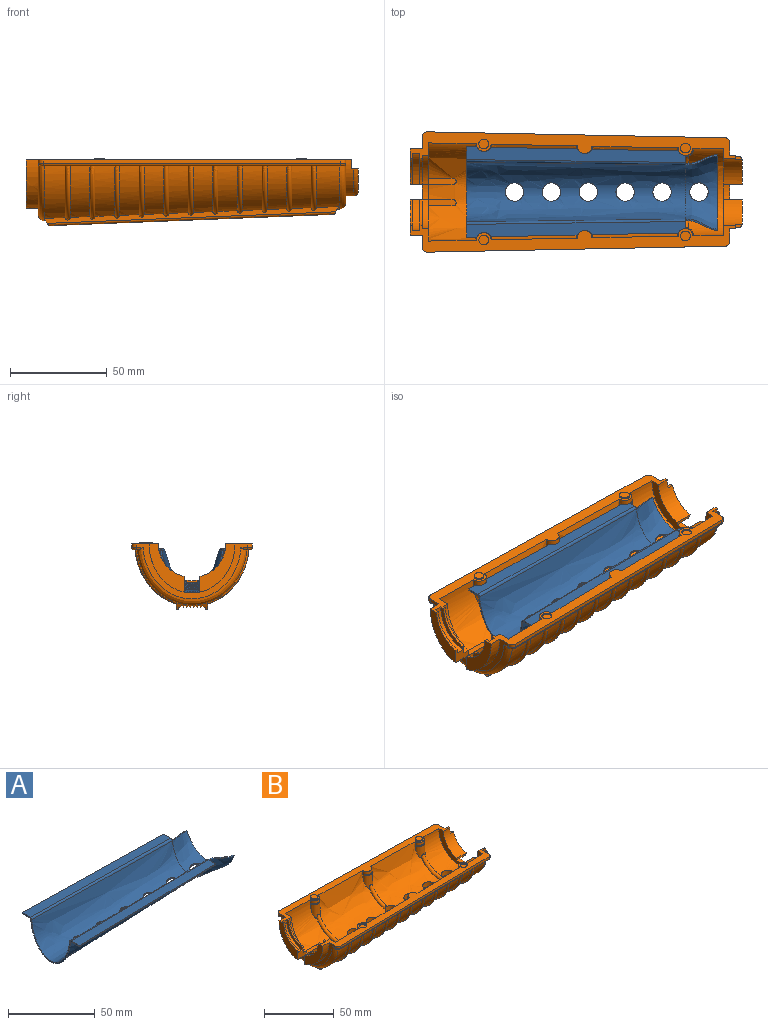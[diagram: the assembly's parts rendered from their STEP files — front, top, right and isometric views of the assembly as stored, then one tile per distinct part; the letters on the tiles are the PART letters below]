
ASSEMBLY  parts=2 mates=1
PART A: 31 faces, bbox 177.5x65.5x54.2 mm
  f0: bspline ~152.4x63.95mm, area 5551mm2, adj f2,f15,f23,f24,f26,f27,f28,f29
  f1: offset ~39.16x18.48mm, area 778.8mm2, adj f7,f8,f9,f25
  f2: bspline ~37.57x16.92mm, area 743.3mm2, adj f0,f7,f8,f9,f25
  f3: plane 6.64x0.79mm, normal (-1,0,0), area 5.3mm2, adj f4,f16,f18,f22
  f4: plane 113.03x2.26mm, normal (0.02,1,0), area 89.7mm2, adj f3,f5,f18,f22
  f5: plane 5.85x0.79mm, normal (1,0,0), area 4.6mm2, adj f4,f6,f18,f22
  f6: bspline ~1.26x1.21mm, area 1mm2, adj f5,f7,f20,f24
  f7: bspline ~16.51x5.3mm, area 14.1mm2, adj f1,f2,f6,f8
  f8: plane 39.09x15.21mm, normal (1,0,0), area 40.2mm2, adj f1,f2,f7,f9
  f9: bspline ~16.51x5.82mm, area 14mm2, adj f1,f2,f8,f10
  f10: bspline ~1.26x1.21mm, area 1mm2, adj f9,f11,f19,f23
  f11: plane 5.84x0.79mm, normal (1,0,0), area 4.6mm2, adj f10,f12,f17,f21
  f12: plane 113.03x2.26mm, normal (0.02,-1,0), area 89.7mm2, adj f11,f13,f17,f21
  f13: plane 6.63x0.79mm, normal (-1,0,0), area 5.3mm2, adj f12,f14,f17,f21
  f14: bspline ~1.26x1.23mm, area 1mm2, adj f13,f15,f19,f23
  f15: bspline ~32.49x21.92mm, area 46.1mm2, adj f0,f14,f16
  f16: bspline ~1.26x1.23mm, area 1mm2, adj f3,f15,f20,f24
  f17: plane 113.03x8.1mm, normal (0,0,-1), area 704.9mm2, adj f11,f12,f13,f19
  f18: plane 113.03x8.11mm, normal (0,0,-1), area 705.5mm2, adj f3,f4,f5,f20
  f19: bspline ~156.83x2.51mm, area 78.8mm2, adj f10,f14,f17
  f20: bspline ~156.83x2.51mm, area 78.7mm2, adj f6,f16,f18
  f21: plane 113.03x8.1mm, normal (0,0,1), area 704.9mm2, adj f11,f12,f13,f23
  f22: plane 113.03x8.11mm, normal (0,0,1), area 705.5mm2, adj f3,f4,f5,f24
  f23: bspline ~156.84x3.3mm, area 210.1mm2, adj f0,f10,f14,f21
  f24: bspline ~156.84x3.3mm, area 209.9mm2, adj f0,f6,f16,f22
  f25: cylinder r=4.76mm len=9.53mm, axis (0,0,1), area 24.6mm2, adj f1,f2
  f26: cylinder r=4.76mm len=9.53mm, axis (0,0,1), area 25.1mm2, adj f0
  f27: cylinder r=4.76mm len=9.53mm, axis (0,0,1), area 25.1mm2, adj f0
  f28: cylinder r=4.76mm len=9.53mm, axis (0,0,1), area 25.1mm2, adj f0
  f29: cylinder r=4.76mm len=9.53mm, axis (0,0,1), area 25.1mm2, adj f0
  f30: cylinder r=4.76mm len=9.53mm, axis (0,0,1), area 25.1mm2, adj f0
PART B: 246 faces, bbox 229.3x149.4x113.7 mm
  f0: cylinder r=17.46mm len=17.01mm, axis (1,0,0), area 29.8mm2, adj f13,f41,f198,f243
  f1: cylinder r=17.46mm len=17.01mm, axis (1,0,0), area 29.8mm2, adj f12,f137,f199,f242
  f2: cone r=3.81mm half-angle=3deg, axis (0,0,-1), area 122.1mm2, adj f13,f15,f40,f204,f237,f238,f239
  f3: cone r=3.81mm half-angle=3deg, axis (0,0,-1), area 132.4mm2, adj f13,f14,f15,f39,f234,f235,f236
  f4: cone r=3.81mm half-angle=3deg, axis (0,0,-1), area 142.5mm2, adj f8,f13,f14,f205,f231,f232,f233
  f5: cone r=3.81mm half-angle=3deg, axis (0,0,-1), area 142.5mm2, adj f8,f12,f14,f205,f228,f229,f230
  f6: cone r=3.81mm half-angle=3deg, axis (0,0,-1), area 132.4mm2, adj f12,f14,f15,f38,f225,f226,f227
  f7: cone r=3.81mm half-angle=3deg, axis (0,0,-1), area 122.1mm2, adj f12,f15,f40,f204,f222,f223,f224
  f8: offset ~81.13x59.72mm, area 2868.9mm2, adj f4,f5,f9,f10,f11,f12,f13,f199
  f9: plane 8.31x3.82mm, normal (1,0,0), area 24.3mm2, adj f8,f197,f199,f217
  f10: plane 28.95x23.02mm, normal (1,0,0), area 200.2mm2, adj f8,f12,f144,f199,f220,f221
  f11: plane 85.09x79.17mm, normal (1,0,0), area 200.2mm2, adj f8,f13,f44,f198,f215,f218
  f12: plane 224.2x69.53mm, normal (0,0,1), area 994.6mm2, adj f1,f5,f6,f7,f8,f10,f14,f15
  f13: plane 226.06x71.39mm, normal (0,0,1), area 994.6mm2, adj f0,f2,f3,f4,f8,f11,f14,f15
  f14: offset ~79.55x57.68mm, area 4950.3mm2, adj f3,f4,f5,f6,f12,f13,f38,f39
  f15: offset ~76.82x55.29mm, area 4608.6mm2, adj f2,f3,f6,f7,f12,f13,f38,f39
  f16: plane 150.68x7.49mm, normal (0.03,-0.71,-0.71), area 182mm2, adj f18,f19,f71,f72,f91,f101,f111,f159
  f17: plane 150.7x7.51mm, normal (0.03,0.71,-0.71), area 181.7mm2, adj f36,f37,f89,f90,f100,f110,f120,f159
  f18: plane 15.79x1.59mm, normal (0.03,0.71,-0.71), area 17.6mm2, adj f16,f21,f173,f206
  f19: plane 15.79x1.59mm, normal (0.03,0.71,-0.71), area 17.6mm2, adj f16,f20,f174,f206
  f20: plane 12.78x1.42mm, normal (0.03,-0.71,-0.71), area 14.9mm2, adj f19,f23,f174,f206
  f21: plane 12.78x1.42mm, normal (0.03,-0.71,-0.71), area 14.9mm2, adj f18,f22,f173,f206
  f22: plane 11.19x1.34mm, normal (0.03,0.71,-0.71), area 13.4mm2, adj f21,f25,f173,f206
  f23: plane 11.19x1.34mm, normal (0.03,0.71,-0.71), area 13.4mm2, adj f20,f24,f174,f206
  f24: plane 10.23x1.3mm, normal (0.03,-0.71,-0.71), area 12.5mm2, adj f23,f27,f174,f206
  f25: plane 10.23x1.3mm, normal (0.03,-0.71,-0.71), area 12.5mm2, adj f22,f26,f173,f206
  f26: plane 9.7x1.28mm, normal (0.03,0.71,-0.71), area 12.1mm2, adj f25,f29,f173,f206
  f27: plane 9.7x1.28mm, normal (0.03,0.71,-0.71), area 12.1mm2, adj f24,f28,f174,f206
  f28: plane 9.7x1.28mm, normal (0.03,-0.71,-0.71), area 12mm2, adj f27,f31,f174,f206
  f29: plane 9.7x1.28mm, normal (0.03,-0.71,-0.71), area 12mm2, adj f26,f30,f173,f206
  f30: plane 10.22x1.3mm, normal (0.03,0.71,-0.71), area 12.5mm2, adj f29,f33,f173,f206
  f31: plane 10.22x1.3mm, normal (0.03,0.71,-0.71), area 12.5mm2, adj f28,f32,f174,f206
  f32: plane 11.18x1.34mm, normal (0.03,-0.71,-0.71), area 13.4mm2, adj f31,f35,f174,f206
  f33: plane 11.18x1.34mm, normal (0.03,-0.71,-0.71), area 13.4mm2, adj f30,f34,f173,f206
  f34: plane 12.75x1.42mm, normal (0.03,0.71,-0.71), area 14.9mm2, adj f33,f37,f173,f206
  f35: plane 12.75x1.42mm, normal (0.03,0.71,-0.71), area 14.9mm2, adj f32,f36,f174,f206
  f36: plane 15.74x1.59mm, normal (0.03,-0.71,-0.71), area 17.6mm2, adj f17,f35,f174,f206
  f37: plane 15.74x1.59mm, normal (0.03,-0.71,-0.71), area 17.6mm2, adj f17,f34,f173,f206
  f38: bspline ~21.22x16.17mm, area 99.1mm2, adj f6,f14,f15,f206
  f39: bspline ~22.14x18.27mm, area 99.1mm2, adj f3,f14,f15,f206
  f40: offset ~74.08x50.66mm, area 1618.4mm2, adj f2,f7,f12,f13,f145,f171,f204
  f41: plane 25.12x18.33mm, normal (-1,0,0), area 172.2mm2, adj f0,f13,f42,f198
  f42: extruded ~24.99x18.26mm, area 212.3mm2, adj f13,f41,f139,f198
  f43: cylinder r=17.46mm len=17.01mm, axis (1,0,0), area 29.8mm2, adj f13,f45,f198,f244
  f44: extruded ~21.73x15.08mm, area 90.3mm2, adj f11,f13,f45,f198
  f45: plane 21.77x15.1mm, normal (1,0,0), area 73.9mm2, adj f13,f43,f44,f198
  f46: cylinder r=19.05mm len=18.63mm, axis (-1,0,0), area 104.4mm2, adj f12,f48,f140,f194,f200,f201
  f47: cylinder r=17.46mm len=17.01mm, axis (1,0,0), area 207.8mm2, adj f12,f48,f145,f194,f200,f201
  f48: torus R=16.83mm, axis (1,0,0), area 57.2mm2, adj f46,f47,f194,f201
  f49: bspline ~158.75x48.38mm, area 298.7mm2, adj f69,f70,f161,f183
  f50: bspline ~158.75x48.89mm, area 304.9mm2, adj f68,f69,f161,f183
  f51: bspline ~158.75x48.89mm, area 311mm2, adj f67,f68,f161,f183
  f52: bspline ~158.75x48.89mm, area 317.1mm2, adj f66,f67,f161,f183
  f53: bspline ~158.75x48.89mm, area 323.2mm2, adj f65,f66,f161,f183
  f54: bspline ~158.75x48.89mm, area 329.3mm2, adj f64,f65,f161,f183
  f55: bspline ~158.75x48.89mm, area 335.4mm2, adj f63,f64,f161,f183
  f56: bspline ~158.75x48.89mm, area 341.6mm2, adj f62,f63,f161,f183
  f57: bspline ~158.75x48.89mm, area 347.7mm2, adj f61,f62,f161,f183
  f58: bspline ~158.75x48.89mm, area 353.8mm2, adj f60,f61,f161,f183
  f59: bspline ~158.75x48.89mm, area 379.3mm2, adj f60,f123,f161,f183
  f60: bspline ~27.95x21.53mm, area 144.9mm2, adj f58,f59,f161,f183
  f61: bspline ~27.44x21.27mm, area 142.5mm2, adj f57,f58,f161,f183
  f62: bspline ~26.93x21.02mm, area 140.1mm2, adj f56,f57,f161,f183
  f63: bspline ~26.42x20.76mm, area 137.6mm2, adj f55,f56,f161,f183
  f64: bspline ~25.91x20.5mm, area 135.2mm2, adj f54,f55,f161,f183
  f65: bspline ~25.4x20.24mm, area 132.8mm2, adj f53,f54,f161,f183
  f66: bspline ~24.89x19.99mm, area 130.4mm2, adj f52,f53,f161,f183
  f67: bspline ~24.38x19.73mm, area 128mm2, adj f51,f52,f161,f183
  f68: bspline ~23.88x19.47mm, area 125.6mm2, adj f50,f51,f161,f183
  f69: bspline ~23.5x19.23mm, area 123.6mm2, adj f49,f50,f161,f183
  f70: bspline ~23x18.97mm, area 121.2mm2, adj f49,f125,f161,f183
  f71: plane 15.79x1.59mm, normal (0.03,0.71,-0.71), area 17.6mm2, adj f16,f74,f174,f175
  f72: plane 41.96x2.62mm, normal (0.03,0.71,-0.71), area 51.2mm2, adj f16,f73,f160,f175
  f73: plane 40.41x2.53mm, normal (0.03,-0.71,-0.71), area 49.9mm2, adj f72,f76,f160,f175
  f74: plane 12.78x1.42mm, normal (0.03,-0.71,-0.71), area 14.9mm2, adj f71,f75,f174,f175
  f75: plane 11.19x1.34mm, normal (0.03,0.71,-0.71), area 13.4mm2, adj f74,f78,f174,f175
  f76: plane 39.61x2.46mm, normal (0.03,0.71,-0.71), area 49.1mm2, adj f73,f77,f160,f175
  f77: plane 39.12x2.44mm, normal (0.03,-0.71,-0.71), area 48.7mm2, adj f76,f80,f160,f175
  f78: plane 10.23x1.3mm, normal (0.03,-0.71,-0.71), area 12.5mm2, adj f75,f79,f174,f175
  f79: plane 9.7x1.28mm, normal (0.03,0.71,-0.71), area 12.1mm2, adj f78,f82,f174,f175
  f80: plane 38.85x2.42mm, normal (0.03,0.71,-0.71), area 48.4mm2, adj f77,f81,f160,f175
  f81: plane 38.85x2.42mm, normal (0.03,-0.71,-0.71), area 48.4mm2, adj f80,f84,f160,f175
  f82: plane 9.7x1.28mm, normal (0.03,-0.71,-0.71), area 12mm2, adj f79,f83,f174,f175
  f83: plane 10.22x1.3mm, normal (0.03,0.71,-0.71), area 12.5mm2, adj f82,f86,f174,f175
  f84: plane 39.11x2.44mm, normal (0.03,0.71,-0.71), area 48.7mm2, adj f81,f85,f160,f175
  f85: plane 39.6x2.46mm, normal (0.03,-0.71,-0.71), area 49.1mm2, adj f84,f88,f160,f175
  f86: plane 11.18x1.34mm, normal (0.03,-0.71,-0.71), area 13.4mm2, adj f83,f87,f174,f175
  f87: plane 12.75x1.42mm, normal (0.03,0.71,-0.71), area 14.9mm2, adj f86,f90,f174,f175
  f88: plane 40.4x2.53mm, normal (0.03,0.71,-0.71), area 49.9mm2, adj f85,f89,f160,f175
  f89: plane 41.93x2.61mm, normal (0.03,-0.71,-0.71), area 51.2mm2, adj f17,f88,f160,f175
  f90: plane 15.74x1.59mm, normal (0.03,-0.71,-0.71), area 17.6mm2, adj f17,f87,f174,f175
  f91: plane 15.79x1.59mm, normal (0.03,0.71,-0.71), area 17.6mm2, adj f16,f92,f172,f173
  f92: plane 12.78x1.42mm, normal (0.03,-0.71,-0.71), area 14.9mm2, adj f91,f93,f172,f173
  f93: plane 11.19x1.34mm, normal (0.03,0.71,-0.71), area 13.4mm2, adj f92,f94,f172,f173
  f94: plane 10.23x1.3mm, normal (0.03,-0.71,-0.71), area 12.5mm2, adj f93,f95,f172,f173
  f95: plane 9.7x1.28mm, normal (0.03,0.71,-0.71), area 12.1mm2, adj f94,f96,f172,f173
  f96: plane 9.7x1.28mm, normal (0.03,-0.71,-0.71), area 12mm2, adj f95,f97,f172,f173
  f97: plane 10.22x1.3mm, normal (0.03,0.71,-0.71), area 12.5mm2, adj f96,f98,f172,f173
  f98: plane 11.18x1.34mm, normal (0.03,-0.71,-0.71), area 13.4mm2, adj f97,f99,f172,f173
  f99: plane 12.75x1.42mm, normal (0.03,0.71,-0.71), area 14.9mm2, adj f98,f100,f172,f173
  f100: plane 15.74x1.59mm, normal (0.03,-0.71,-0.71), area 17.6mm2, adj f17,f99,f172,f173
  f101: plane 15.79x1.59mm, normal (0.03,0.71,-0.71), area 17.6mm2, adj f16,f102,f171,f172
  f102: plane 12.78x1.42mm, normal (0.03,-0.71,-0.71), area 14.9mm2, adj f101,f103,f171,f172
  f103: plane 11.19x1.34mm, normal (0.03,0.71,-0.71), area 13.4mm2, adj f102,f104,f171,f172
  f104: plane 10.23x1.3mm, normal (0.03,-0.71,-0.71), area 12.5mm2, adj f103,f105,f171,f172
  f105: plane 9.7x1.28mm, normal (0.03,0.71,-0.71), area 12.1mm2, adj f104,f106,f171,f172
  f106: plane 9.7x1.28mm, normal (0.03,-0.71,-0.71), area 12mm2, adj f105,f107,f171,f172
  f107: plane 10.22x1.3mm, normal (0.03,0.71,-0.71), area 12.5mm2, adj f106,f108,f171,f172
  f108: plane 11.18x1.34mm, normal (0.03,-0.71,-0.71), area 13.4mm2, adj f107,f109,f171,f172
  f109: plane 12.75x1.42mm, normal (0.03,0.71,-0.71), area 14.9mm2, adj f108,f110,f171,f172
  f110: plane 15.74x1.59mm, normal (0.03,-0.71,-0.71), area 17.6mm2, adj f17,f109,f171,f172
  f111: plane 9.71x1.4mm, normal (0.03,0.71,-0.71), area 10.7mm2, adj f16,f112,f159,f171
  f112: plane 8.17x1.23mm, normal (0.03,-0.71,-0.71), area 9.4mm2, adj f111,f113,f159,f171
  f113: plane 7.36x1.21mm, normal (0.03,0.71,-0.71), area 8.6mm2, adj f112,f114,f159,f171
  f114: plane 6.88x1.17mm, normal (0.03,-0.71,-0.71), area 8.1mm2, adj f113,f115,f159,f171
  f115: plane 6.6x1.16mm, normal (0.03,0.71,-0.71), area 7.9mm2, adj f114,f116,f159,f171
  f116: plane 6.6x1.16mm, normal (0.03,-0.71,-0.71), area 7.9mm2, adj f115,f117,f159,f171
  f117: plane 6.87x1.17mm, normal (0.03,0.71,-0.71), area 8.1mm2, adj f116,f118,f159,f171
  f118: plane 7.35x1.21mm, normal (0.03,-0.71,-0.71), area 8.6mm2, adj f117,f119,f159,f171
  f119: plane 8.16x1.23mm, normal (0.03,0.71,-0.71), area 9.4mm2, adj f118,f120,f159,f171
  f120: plane 9.68x1.4mm, normal (0.03,-0.71,-0.71), area 10.7mm2, adj f17,f119,f159,f171
  f121: plane 147.56x5.9mm, normal (0.04,0,-1), area 1.5mm2, adj f159,f160,f166,f170
  f122: bspline ~13.71x0.92mm, area 0mm2, adj f123,f160
  f123: bspline ~56.9x29.7mm, area 432.6mm2, adj f59,f122,f135,f139,f160,f161,f162,f179
  f124: bspline ~158.75x48.38mm, area 298.7mm2, adj f157,f158,f162,f179
  f125: bspline ~51.03x22.88mm, area 706.8mm2, adj f70,f141,f158,f159,f161,f162,f179,f183
  f126: bspline ~158.75x48.89mm, area 304.9mm2, adj f156,f157,f162,f179
  f127: bspline ~158.75x48.89mm, area 311mm2, adj f155,f156,f162,f179
  f128: bspline ~158.75x48.89mm, area 317.1mm2, adj f154,f155,f162,f179
  f129: bspline ~158.75x48.89mm, area 323.2mm2, adj f153,f154,f162,f179
  f130: bspline ~158.75x48.89mm, area 329.3mm2, adj f152,f153,f162,f179
  f131: bspline ~158.75x48.89mm, area 335.4mm2, adj f151,f152,f162,f179
  f132: bspline ~158.75x48.89mm, area 341.6mm2, adj f150,f151,f162,f179
  f133: bspline ~158.75x48.89mm, area 347.7mm2, adj f149,f150,f162,f179
  f134: bspline ~158.75x48.89mm, area 353.8mm2, adj f148,f149,f162,f179
  f135: bspline ~158.75x48.89mm, area 379.3mm2, adj f123,f148,f162,f179
  f136: cylinder r=19.05mm len=18.63mm, axis (-1,0,0), area 104.4mm2, adj f13,f140,f147,f195,f202,f203
  f137: plane 25.12x18.34mm, normal (-1,0,0), area 172mm2, adj f1,f12,f138,f199
  f138: extruded ~24.99x18.26mm, area 212.3mm2, adj f12,f137,f139,f199
  f139: plane 57.08x28.48mm, normal (-1,0,0), area 258.6mm2, adj f12,f13,f42,f123,f138,f178,f180,f184
  f140: plane 50.9x22.35mm, normal (1,0,0), area 224.7mm2, adj f12,f13,f46,f136,f141,f176,f182,f188
  f141: bspline ~50.92x26.25mm, area 345.2mm2, adj f125,f140,f179,f183,f188,f193
  f142: cylinder r=17.46mm len=17.01mm, axis (1,0,0), area 29.8mm2, adj f12,f146,f199,f241
  f143: cylinder r=17.46mm len=17.01mm, axis (1,0,0), area 207.8mm2, adj f13,f145,f147,f195,f202,f203
  f144: extruded ~21.73x15.08mm, area 90.3mm2, adj f10,f12,f146,f199
  f145: plane 93.65x71.43mm, normal (-1,0,0), area 290.8mm2, adj f12,f13,f40,f47,f143,f194,f195,f196
  f146: plane 21.77x15.1mm, normal (1,0,0), area 73.9mm2, adj f12,f142,f144,f199
  f147: torus R=16.83mm, axis (1,0,0), area 57.2mm2, adj f136,f143,f195,f202
  f148: bspline ~27.95x21.53mm, area 144.9mm2, adj f134,f135,f162,f179
  f149: bspline ~27.44x21.27mm, area 142.5mm2, adj f133,f134,f162,f179
  f150: bspline ~26.93x21.02mm, area 140.1mm2, adj f132,f133,f162,f179
  f151: bspline ~26.42x20.76mm, area 137.6mm2, adj f131,f132,f162,f179
  f152: bspline ~25.91x20.5mm, area 135.2mm2, adj f130,f131,f162,f179
  f153: bspline ~25.4x20.24mm, area 132.8mm2, adj f129,f130,f162,f179
  f154: bspline ~24.89x19.99mm, area 130.4mm2, adj f128,f129,f162,f179
  f155: bspline ~24.38x19.73mm, area 128mm2, adj f127,f128,f162,f179
  f156: bspline ~23.88x19.47mm, area 125.6mm2, adj f126,f127,f162,f179
  f157: bspline ~23.5x19.23mm, area 123.6mm2, adj f124,f126,f162,f179
  f158: bspline ~23x18.97mm, area 121.2mm2, adj f124,f125,f162,f179
  f159: plane 17.98x5.47mm, normal (0.89,0,-0.46), area 29.4mm2, adj f16,f17,f111,f112,f113,f114,f115,f116
  f160: plane 17.65x4.94mm, normal (-0.85,0,-0.53), area 29.3mm2, adj f16,f17,f72,f73,f76,f77,f80,f81
  f161: plane 152.07x8.66mm, normal (0,1,0), area 367.3mm2, adj f49,f50,f51,f52,f53,f54,f55,f56
  f162: plane 152.07x8.66mm, normal (0,-1,0), area 367.3mm2, adj f123,f124,f125,f126,f127,f128,f129,f130
  f163: plane 150.05x6.87mm, normal (0.03,0.71,-0.71), area 188.1mm2, adj f16,f159,f160,f168
  f164: plane 150.05x6.87mm, normal (0.03,-0.71,-0.71), area 188.1mm2, adj f17,f159,f160,f165
  f165: plane 149.03x5.96mm, normal (0.04,0,-1), area 112.9mm2, adj f159,f160,f164,f166
  f166: plane 149.03x7.2mm, normal (0,-1,0), area 188.3mm2, adj f121,f159,f160,f165
  f167: plane 149.03x7.2mm, normal (0,1,0), area 188.3mm2, adj f159,f160,f168,f169
  f168: plane 149.03x5.96mm, normal (0.04,0,-1), area 112.9mm2, adj f159,f160,f163,f167
  f169: cylinder r=1.27mm len=149.08mm, axis (-1,0,-0.04), area 296.1mm2, adj f159,f160,f162,f167
  f170: cylinder r=1.27mm len=149.08mm, axis (1,0,0.04), area 296.1mm2, adj f121,f159,f160,f161
  f171: cylinder r=4.76mm len=9.53mm, axis (0,0,1), area 127.8mm2, adj f16,f17,f40,f101,f102,f103,f104,f105
  f172: cylinder r=4.76mm len=9.53mm, axis (0,0,1), area 125.7mm2, adj f15,f16,f17,f91,f92,f93,f94,f95
  f173: cylinder r=4.76mm len=9.53mm, axis (0,0,1), area 127.8mm2, adj f15,f16,f17,f18,f21,f22,f25,f26
  f174: cylinder r=4.76mm len=9.53mm, axis (0,0,1), area 125.7mm2, adj f14,f16,f17,f19,f20,f23,f24,f27
  f175: cylinder r=4.76mm len=9.53mm, axis (0,0,1), area 125.7mm2, adj f14,f16,f17,f71,f72,f73,f74,f75
  f176: cylinder r=2.54mm len=2.54mm, axis (0,0,1), area 7.5mm2, adj f12,f140,f177,f187
  f177: plane 153.67x3.07mm, normal (0.02,-1,0), area 292.8mm2, adj f12,f176,f178,f186
  f178: cylinder r=2.54mm len=2.59mm, axis (0,0,1), area 7.7mm2, adj f12,f139,f177,f185
  f179: plane 156.65x5.61mm, normal (0,0,-1), area 196.5mm2, adj f123,f124,f125,f126,f127,f128,f129,f130
  f180: cylinder r=2.54mm len=2.59mm, axis (0,0,1), area 7.7mm2, adj f13,f139,f181,f190
  f181: plane 153.67x3.07mm, normal (0.02,1,0), area 292.8mm2, adj f13,f180,f182,f191
  f182: cylinder r=2.54mm len=2.54mm, axis (0,0,1), area 7.5mm2, adj f13,f140,f181,f192
  f183: plane 156.65x5.61mm, normal (0,0,-1), area 196.5mm2, adj f49,f50,f51,f52,f53,f54,f55,f56
  f184: cylinder r=1.27mm len=3.24mm, axis (0,-1,0), area 4mm2, adj f123,f139,f179,f185
  f185: torus R=1.27mm, axis (0,0,-1), area 6.6mm2, adj f178,f179,f184,f186
  f186: cylinder r=1.27mm len=153.7mm, axis (1,0.02,0), area 306.6mm2, adj f177,f179,f185,f187
  f187: torus R=1.27mm, axis (0,0,-1), area 6.4mm2, adj f176,f179,f186,f188
  f188: cylinder r=1.27mm len=3.24mm, axis (0,-1,0), area 4.1mm2, adj f140,f141,f179,f187
  f189: cylinder r=1.27mm len=3.24mm, axis (0,1,0), area 4mm2, adj f123,f139,f183,f190
  f190: torus R=1.27mm, axis (0,0,-1), area 6.6mm2, adj f180,f183,f189,f191
  f191: cylinder r=1.27mm len=153.7mm, axis (-1,0.02,0), area 306.6mm2, adj f181,f183,f190,f192
  f192: torus R=1.27mm, axis (0,0,-1), area 6.4mm2, adj f182,f183,f191,f193
  f193: cylinder r=1.27mm len=3.24mm, axis (0,1,0), area 4.1mm2, adj f140,f141,f183,f192
  f194: plane 9.7x1.8mm, normal (0,1,0), area 14.6mm2, adj f46,f47,f48,f145,f196
  f195: plane 9.7x1.8mm, normal (0,-1,0), area 14.6mm2, adj f136,f143,f145,f147,f196
  f196: cylinder r=19.05mm len=7.94mm, axis (-1,0,0), area 25.4mm2, adj f140,f145,f194,f195
  f197: extruded ~7.94x3.18mm, area 25.4mm2, adj f9,f139,f198,f199
  f198: plane 9.53x7.98mm, normal (0,-1,0), area 52.4mm2, adj f0,f11,f41,f42,f43,f44,f45,f197
  f199: plane 22.23x11.09mm, normal (0,1,0), area 88.6mm2, adj f1,f8,f9,f10,f137,f138,f142,f144
  f200: plane 4.76x2.25mm, normal (1,0,0), area 7.6mm2, adj f12,f46,f47,f201
  f201: plane 3.38x1.85mm, normal (0,0,1), area 4.3mm2, adj f46,f47,f48,f200
  f202: plane 3.38x1.86mm, normal (0,0,1), area 4.3mm2, adj f136,f143,f147,f203
  f203: plane 4.76x2.25mm, normal (1,0,0), area 7.6mm2, adj f13,f136,f143,f202
  f204: bspline ~43.88x15.67mm, area 220.8mm2, adj f2,f7,f15,f40
  f205: bspline ~47.58x17.94mm, area 252.5mm2, adj f4,f5,f8,f14
  f206: cylinder r=4.76mm len=9.53mm, axis (0,0,1), area 142.2mm2, adj f14,f15,f16,f17,f18,f19,f20,f21
  f207: cylinder r=2.54mm len=5.08mm, axis (0,0,-1), area 12.7mm2, adj f13,f208
  f208: plane 5.08x5.08mm, normal (0,0,1), area 20.3mm2, adj f207
  f209: cylinder r=2.54mm len=5.08mm, axis (0,0,-1), area 12.7mm2, adj f13,f210
  f210: plane 5.08x5.08mm, normal (0,0,1), area 20.3mm2, adj f209
  f211: cylinder r=2.54mm len=5.08mm, axis (0,0,1), area 12.7mm2, adj f12,f212
  f212: plane 5.08x5.08mm, normal (0,0,1), area 20.3mm2, adj f211
  f213: cylinder r=2.54mm len=5.08mm, axis (0,0,1), area 12.7mm2, adj f12,f214
  f214: plane 5.08x5.08mm, normal (0,0,1), area 20.3mm2, adj f213
  f215: plane 13.89x3.49mm, normal (0,1,0), area 26mm2, adj f8,f11,f216,f218
  f216: cylinder r=1.59mm len=3.18mm, axis (0,0,1), area 11mm2, adj f8,f215,f217,f218
  f217: plane 13.04x3.45mm, normal (0,-1,0), area 36.2mm2, adj f8,f9,f216,f218
  f218: plane 14.29x3.18mm, normal (0,0,1), area 44.3mm2, adj f11,f215,f216,f217
  f219: cylinder r=1.59mm len=3.18mm, axis (0,0,1), area 11mm2, adj f8,f199,f220,f221
  f220: plane 12.7x2.31mm, normal (0,-1,0), area 26mm2, adj f8,f10,f219,f221
  f221: plane 14.29x3.18mm, normal (0,0,1), area 44.3mm2, adj f10,f199,f219,f220
  f222: plane 7.22x2.43mm, normal (0,0,-1), area 12.3mm2, adj f7,f224
  f223: plane 7.31x2.47mm, normal (0,0,1), area 12.6mm2, adj f7,f224
  f224: plane 7.31x0.79mm, normal (-0.02,1,0), area 5.8mm2, adj f7,f222,f223
  f225: plane 7.22x2.43mm, normal (0,0,-1), area 12.3mm2, adj f6,f227
  f226: plane 7.31x2.47mm, normal (0,0,1), area 12.6mm2, adj f6,f227
  f227: plane 7.31x0.79mm, normal (-0.02,1,0), area 5.8mm2, adj f6,f225,f226
  f228: plane 7.22x2.43mm, normal (0,0,-1), area 12.3mm2, adj f5,f230
  f229: plane 7.31x2.47mm, normal (0,0,1), area 12.6mm2, adj f5,f230
  f230: plane 7.31x0.79mm, normal (-0.02,1,0), area 5.8mm2, adj f5,f228,f229
  f231: plane 7.22x2.43mm, normal (0,0,-1), area 12.3mm2, adj f4,f233
  f232: plane 7.31x2.47mm, normal (0,0,1), area 12.6mm2, adj f4,f233
  f233: plane 7.31x0.79mm, normal (-0.02,-1,0), area 5.8mm2, adj f4,f231,f232
  f234: plane 7.22x2.43mm, normal (0,0,-1), area 12.3mm2, adj f3,f236
  f235: plane 7.31x2.47mm, normal (0,0,1), area 12.6mm2, adj f3,f236
  f236: plane 7.31x0.79mm, normal (-0.02,-1,0), area 5.8mm2, adj f3,f234,f235
  f237: plane 7.31x0.79mm, normal (-0.02,-1,0), area 5.8mm2, adj f2,f238,f239
  f238: plane 7.31x2.47mm, normal (0,0,1), area 12.6mm2, adj f2,f237
  f239: plane 7.22x2.43mm, normal (0,0,-1), area 12.3mm2, adj f2,f237
  f240: cylinder r=19.69mm len=19.28mm, axis (1,0,0), area 102.6mm2, adj f12,f199,f241,f242
  f241: plane 19.28x15.72mm, normal (-1,0,0), area 56mm2, adj f12,f142,f199,f240
  f242: plane 19.28x15.72mm, normal (1,0,0), area 56mm2, adj f1,f12,f199,f240
  f243: plane 19.28x15.72mm, normal (1,0,0), area 56mm2, adj f0,f13,f198,f245
  f244: plane 19.28x15.72mm, normal (-1,0,0), area 56mm2, adj f13,f43,f198,f245
  f245: cylinder r=19.69mm len=19.28mm, axis (1,0,0), area 102.6mm2, adj f13,f198,f243,f244
PLACE A t=(0,0,-0.01)mm
PLACE B at identity fixed
MATE fastened A.f25 <-> B.f171  axis (0,0,1) through (-225.42,0,-20.29)mm
